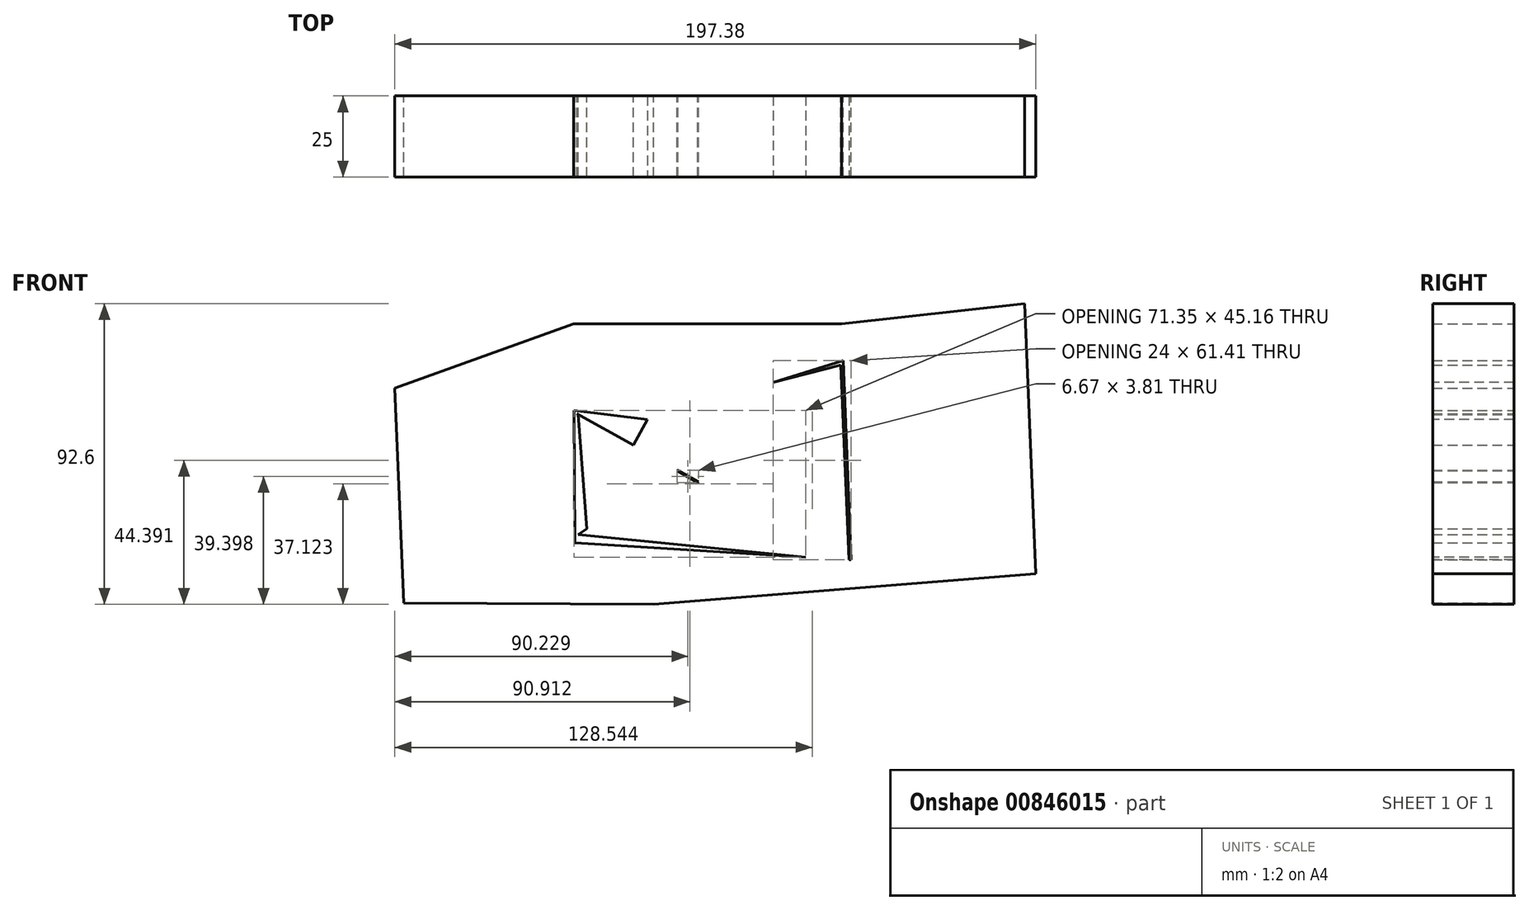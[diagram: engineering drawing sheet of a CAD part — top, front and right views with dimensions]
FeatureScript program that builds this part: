
annotation { "Feature Type Name" : "Feature", "Feature Type Description" : "" }
export const myFeature = defineFeature(function(context is Context, id is Id, definition is map)
    precondition{}
    {
        {
            var Q0;
            Q0=qCreatedBy(makeId("Front.planeOp"),FACE);
            var sketch = newSketch(context, id + "F0", { "sketchPlane" : qUnion([Q0])});
            skLineSegment(sketch, "E0", {"start": v(-49.4, 38.8) * mm, "end": v(33.1, 38.8) * mm});
            skLineSegment(sketch, "E1", {"start": v(33.1, 38.8) * mm, "end": v(36.03, -33.91) * mm});
            skLineSegment(sketch, "E2", {"start": v(36.03, -33.91) * mm, "end": v(-49.08, -28.7) * mm});
            skLineSegment(sketch, "E3", {"start": v(-49.08, -28.7) * mm, "end": v(-49.4, 38.8) * mm});
            skLineSegment(sketch, "E4", {"start": v(33.1, 38.8) * mm, "end": v(89.51, 45) * mm});
            skLineSegment(sketch, "E5", {"start": v(89.51, 45) * mm, "end": v(92.87, -38.12) * mm});
            skLineSegment(sketch, "E6", {"start": v(92.87, -38.12) * mm, "end": v(36.03, -33.91) * mm});
            skLineSegment(sketch, "E7", {"start": v(-49.4, 38.8) * mm, "end": v(-104.51, 18.91) * mm});
            skLineSegment(sketch, "E8", {"start": v(-104.51, 18.91) * mm, "end": v(-101.84, -47.24) * mm});
            skLineSegment(sketch, "E9", {"start": v(-101.84, -47.24) * mm, "end": v(-49.08, -28.7) * mm});
            skLineSegment(sketch, "E10", {"start": v(-104.51, 18.91) * mm, "end": v(-25.15, 9.13) * mm});
            skLineSegment(sketch, "E11", {"start": v(-25.15, 9.13) * mm, "end": v(-24.88, -47.6) * mm});
            skLineSegment(sketch, "E12", {"start": v(-24.88, -47.6) * mm, "end": v(-101.84, -47.24) * mm});
            skLineSegment(sketch, "E13", {"start": v(89.51, 45) * mm, "end": v(-25.15, 9.13) * mm});
            skLineSegment(sketch, "E14", {"start": v(-24.88, -47.6) * mm, "end": v(92.87, -38.12) * mm});
            skSolve(sketch);
        }
        {
            var Q0;
            Q0 = qSketchRegion(id + "F0", true);
            extrude(context, id + "F1", {"entities" : qUnion([Q0]), "depth" : 25 * mm, "offsetDistance" : 25 * mm});
        }
        {
            var Q0;
            Q0=qCreatedBy(makeId("Front.planeOp"),FACE);
            var sketch = newSketch(context, id + "F2", { "sketchPlane" : qUnion([Q0])});
            skLineSegment(sketch, "E15", {"start": v(-48.38, 11.09) * mm, "end": v(-11.2, -10.1) * mm});
            skLineSegment(sketch, "E16", {"start": v(-11.2, -10.1) * mm, "end": v(32.82, 26.09) * mm});
            skLineSegment(sketch, "E17", {"start": v(32.82, 26.09) * mm, "end": v(35.43, -35.87) * mm});
            skLineSegment(sketch, "E18", {"start": v(35.43, -35.87) * mm, "end": v(-13.28, -8.93) * mm});
            skLineSegment(sketch, "E19", {"start": v(-13.28, -8.93) * mm, "end": v(-48.05, -26.09) * mm});
            skLineSegment(sketch, "E20", {"start": v(-48.05, -26.09) * mm, "end": v(32.15, -34.06) * mm});
            skLineSegment(sketch, "E21", {"start": v(32.15, -34.06) * mm, "end": v(-48.38, 11.09) * mm});
            skLineSegment(sketch, "E22", {"start": v(-48.05, -26.09) * mm, "end": v(32.82, 26.09) * mm});
            skLineSegment(sketch, "E23", {"start": v(-48.05, 10.9) * mm, "end": v(-45.35, -24.34) * mm});
            skLineSegment(sketch, "E24", {"start": v(-45.35, -24.34) * mm, "end": v(-25.75, 11.09) * mm});
            skLineSegment(sketch, "E25", {"start": v(-25.75, 11.09) * mm, "end": v(32.82, 26.09) * mm});
            skSolve(sketch);
        }
        {
            var Q0;
            Q0 = qSketchRegion(id + "F2", true);
            extrude(context, id + "F3", {"entities" : qUnion([Q0]), "operationType" : NewBodyOperationType.ADD, "depth" : 25 * mm, "offsetDistance" : 25 * mm});
        }
    });
